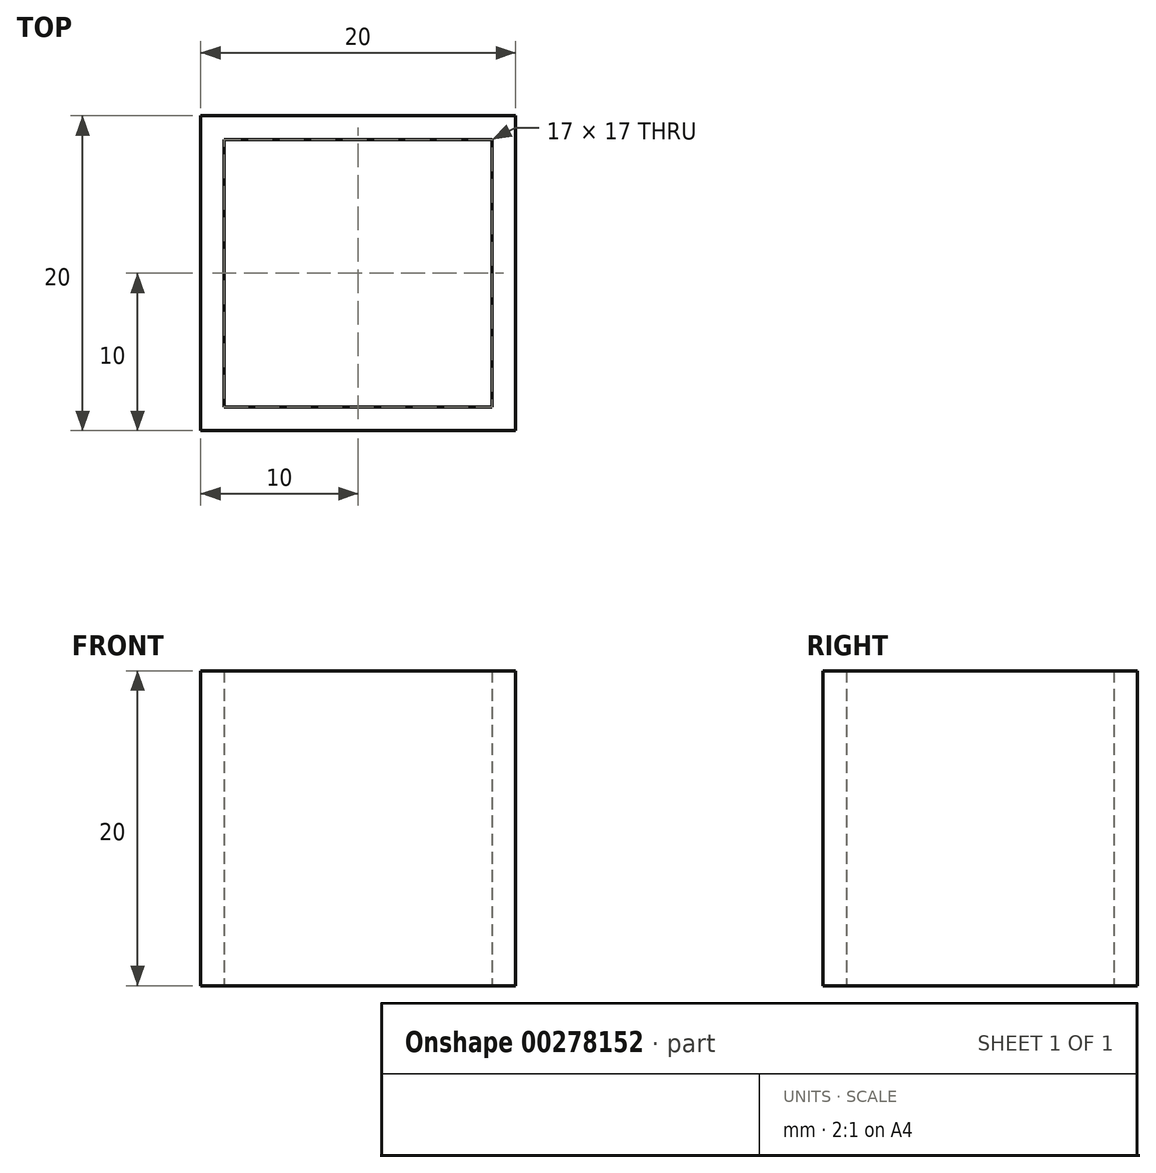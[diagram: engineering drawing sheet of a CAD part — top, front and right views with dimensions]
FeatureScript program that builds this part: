
annotation { "Feature Type Name" : "Feature", "Feature Type Description" : "" }
export const myFeature = defineFeature(function(context is Context, id is Id, definition is map)
    precondition{}
    {
        {
            var Q0;
            Q0=qCreatedBy(makeId("Top.planeOp"),FACE);
            var sketch = newSketch(context, id + "F0", { "sketchPlane" : qUnion([Q0])});
            skLineSegment(sketch, "E0.bottom", {"start": v(-8.5, 8.5) * mm, "end": v(8.5, 8.5) * mm});
            skLineSegment(sketch, "E0.top", {"start": v(-8.5, -8.5) * mm, "end": v(8.5, -8.5) * mm});
            skLineSegment(sketch, "E0.left", {"start": v(-8.5, 8.5) * mm, "end": v(-8.5, -8.5) * mm});
            skLineSegment(sketch, "E0.right", {"start": v(8.5, 8.5) * mm, "end": v(8.5, -8.5) * mm});
            skPoint(sketch, "E0.middle", {"position": v(0, 0) * mm});
            skLineSegment(sketch, "E1.bottom", {"start": v(-10, 10) * mm, "end": v(10, 10) * mm});
            skLineSegment(sketch, "E1.top", {"start": v(-10, -10) * mm, "end": v(10, -10) * mm});
            skLineSegment(sketch, "E1.left", {"start": v(-10, 10) * mm, "end": v(-10, -10) * mm});
            skLineSegment(sketch, "E1.right", {"start": v(10, 10) * mm, "end": v(10, -10) * mm});
            skSolve(sketch);
        }
        {
            var Q0;
            Q0=makeQuery(id+"F0.imprint","IMPRINT",FACE,{"disambiguationData":[TD([[makeQuery(id+"F0.imprint","IMPRINT",EDGE,{"derivedFrom":sQuery(id+"F0.wireOp",EDGE,"E0.bottom")}),1.0]])]});
            extrude(context, id + "F1", {"entities" : qUnion([Q0]), "depth" : 20 * mm});
        }
    });
